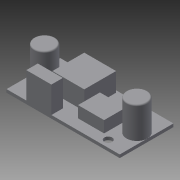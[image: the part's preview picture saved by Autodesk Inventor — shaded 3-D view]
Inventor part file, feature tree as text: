
AUTODESK INVENTOR PART (.ipt)
format: ipt  version: 2016 (Build 200138000, 138)  size: 153,088 bytes
history: native  units: in
note: dims shown in document units (in); Inventor stores cm internally (conversion verified against a paired STEP export)
features: extrude x6, sketch x6, fillet x1
ambient origin geometry x8: Origin, YZ Plane, XZ Plane, XY Plane, X Axis, Y Axis, Z Axis, Center Point
bodies: Solid1 (feature_tree)
feature tree (13):
  extrude  "Extrusion1"  Depth=0.811in
  extrude  "Extrusion2"  Depth=0.315in
  fillet  "Fillet1"  Radius=0.3937in
  extrude  "Extrusion3"  Depth=0.1575in
  extrude  "Extrusion4"  Depth=0.4724in TaperAngle=0.0deg
  extrude  "Extrusion5"  Depth=0.378in
  extrude  "Extrusion6"  TaperAngle=0.0deg  [1 undecoded]
  sketch  "Sketch1"  dims[d0=1.7087in d1=0.811in]
  sketch  "Sketch2"  dims[d2=0.0472in d3=0.0in d4=0.315in d5=0.3937in]
  sketch  "Sketch3"  dims[d6=0.315in d7=0.1575in]
  sketch  "Sketch4"  dims[d8=0.1575in d9=0.4724in d10=0.0in]
  sketch  "Sketch5"  dims[d11=0.0197in d12=0.378in]
  sketch  "Sketch6"  dims[d13=0.1732in d14=0.0in d15=0.2992in d16=0.3976in d17=0.0in d18=0.1181in d19=0.2795in d20=0.1063in d21=0.1181in d22=0.1063in d23=0.2559in d24=0.3976in d25=0.0in d26=0.4803in d27=0.4803in d28=0.0315in d29=0.3937in d30=0.2835in d31=0.0in d32=0.3937in d33=0.3307in d34=0.1575in d35=0.3937in d36=0.1732in d37=0.0in]
note: 1 required parameter value undecoded (feature->parameter linkage not recoverable at this tier; creation-order binding heuristic only, values carry confidence <= 0.55)
